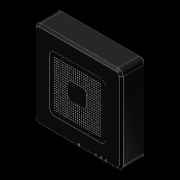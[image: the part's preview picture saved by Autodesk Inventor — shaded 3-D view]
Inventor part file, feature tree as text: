
AUTODESK INVENTOR PART (.ipt)
format: ipt  version: 2012 (Build 160160000, 160)  size: 2,737,152 bytes
history: native  units: in
note: dims shown in document units (in); Inventor stores cm internally (conversion verified against a paired STEP export)
features: extrude x10, sketch x10, chamfer x1, fillet x1, plane x1, mirror x1
ambient origin geometry x8: Origin, YZ Plane, XZ Plane, XY Plane, X Axis, Y Axis, Z Axis, Center Point
bodies: Solid1 (feature_tree)
feature tree (24):
  extrude  "Extrusion1"  Depth=4.3375in
  chamfer  "Chamfer1"  Distance=0.165in
  extrude  "Extrusion2"  Depth=0.68in
  extrude  "Extrusion3"  Depth=0.68in
  extrude  "Extrusion4"  Depth=0.25in
  extrude  "Extrusion5"  Depth=0.05in
  extrude  "Extrusion7"  Depth=0.0in TaperAngle=0.0deg
  fillet  "Fillet1"  Radius=0.16in
  extrude  "Extrusion9"  Depth=0.015in TaperAngle=0.0deg
  plane  "Work Plane2"
  mirror  "Mirror1"
  extrude  "Extrusion10"  Depth=0.93in TaperAngle=0.0deg
  extrude  "Extrusion11"  Depth=0.065in
  extrude  "Extrusion12"  Depth=0.45in
  sketch  "Sketch1"  dims[d0=4.3375in d1=4.3375in]
  sketch  "Sketch2"  dims[d2=0.25in d3=0.165in d4=0.0in]
  sketch  "Sketch3"  dims[d5=0.1in d6=0.1in d7=45.0deg d8=0.68in]
  sketch  "Sketch4"  dims[d9=0.68in d10=0.68in]
  sketch  "Sketch5"  dims[d11=0.68in d12=0.25in]
  sketch  "Sketch6"  dims[d13=0.0125in d14=0.0in d15=0.05in]
  sketch  "Sketch8"  dims[d16=9.0551in d18=0.103in d19=9.0551in d21=0.103in d24=0.0in d25=0.0in d26=0.16in d27=0.0in]
  sketch  "Sketch9"  dims[d28=0.05in d29=0.0in d32=0.015in d33=0.0in]
  sketch  "Sketch10"  dims[d34=0.125in d37=0.93in d38=0.0in]
  sketch  "Sketch11"  dims[d40=0.565in d42=0.065in d43=0.45in d44=0.1in d45=1.1811in d47=0.25in d48=0.3937in d50=1.0in d52=0.7874in d54=0.87in d55=0.3937in d57=1.0in d59=0.095in d60=0.0in d61=0.01in d62=0.01in d63=0.095in d64=0.0in d65=0.0in d66=0.0in]
